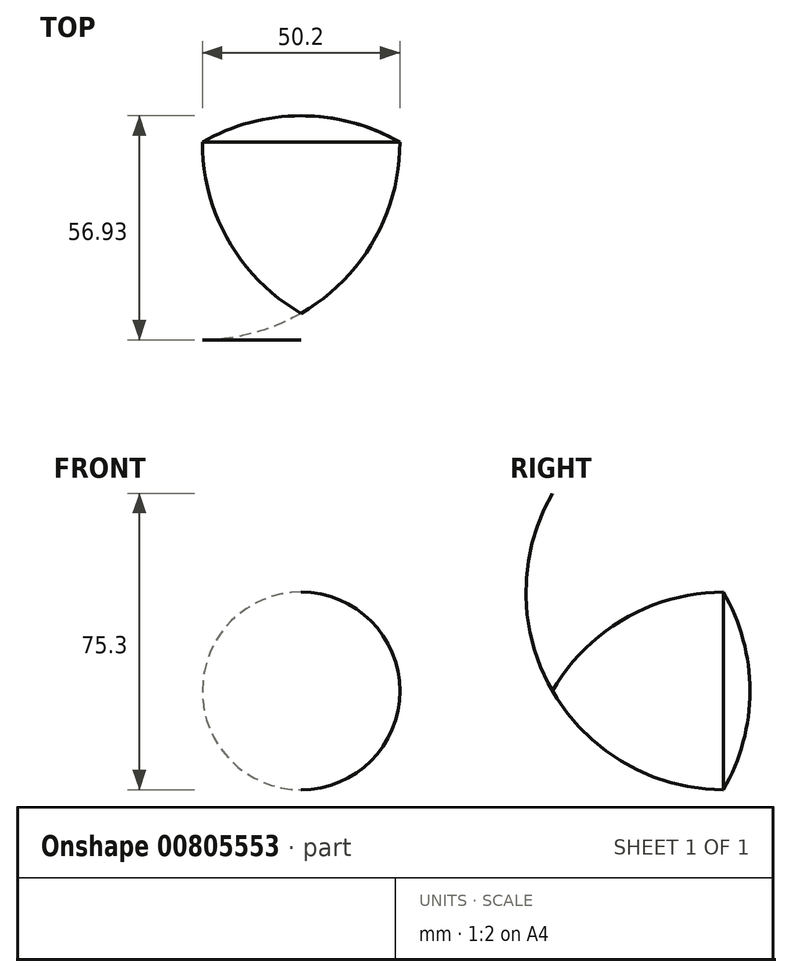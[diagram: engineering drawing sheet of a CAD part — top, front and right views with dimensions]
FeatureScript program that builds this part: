
annotation { "Feature Type Name" : "Feature", "Feature Type Description" : "" }
export const myFeature = defineFeature(function(context is Context, id is Id, definition is map)
    precondition{}
    {
        {
            var Q0;
            Q0=qCreatedBy(makeId("Top.planeOp"),FACE);
            var sketch = newSketch(context, id + "F0", { "sketchPlane" : qUnion([Q0])});
            skLineSegment(sketch, "E0.0", {"start": v(-25.1, 14.5) * mm, "end": v(0, 14.5) * mm});
            skLineSegment(sketch, "E0.2", {"start": v(0, -28.98) * mm, "end": v(-25.1, 14.5) * mm});
            skPoint(sketch, "E0.0.midPoint", {"position": v(0, 14.5) * mm});
            skArc(sketch, "E1", {"start": v(-25.1, 14.5) * mm, "mid": v(-18.37, -10.6) * mm, "end": v(0, -28.98) * mm});
            skArc(sketch, "E2", {"start": v(0, 21.22) * mm, "mid": v(-13, 19.5) * mm, "end": v(-25.1, 14.5) * mm});
            skLineSegment(sketch, "E3", {"start": v(0, 21.22) * mm, "end": v(0, -28.98) * mm});
            skSolve(sketch);
        }
        {
            var Q0;
            {var subQ0=sQuery(id+"F0.wireOp",EDGE,"E0.0");Q0=makeQuery(id+"F0.imprint","IMPRINT",FACE,{"disambiguationData":[TD([[makeQuery(id+"F0.imprint","IMPRINT",EDGE,{"derivedFrom":subQ0}),-1.0]])]});}
            var Q1;
            Q1=makeQuery(id+"F0.imprint","IMPRINT",FACE,{"disambiguationData":[TD([[makeQuery(id+"F0.imprint","IMPRINT",EDGE,{"derivedFrom":sQuery(id+"F0.wireOp",EDGE,"E0.2")}),1.0]])]});
            var Q2;
            {var subQ0=sQuery(id+"F0.wireOp",EDGE,"E0.0");Q2=makeQuery(id+"F0.imprint","IMPRINT",FACE,{"disambiguationData":[TD([[makeQuery(id+"F0.imprint","IMPRINT",EDGE,{"derivedFrom":subQ0}),1.0]])]});}
            var Q3;
            Q3=sQuery(id+"F0.wireOp",EDGE,"E3");
            revolve(context, id + "F1", {"surfaceOperationType" : NewSurfaceOperationType.NEW, "entities" : qUnion([Q0, Q1, Q2]), "axis" : qUnion([Q3]), "revolveType" : RevolveType.FULL});
        }
    });
